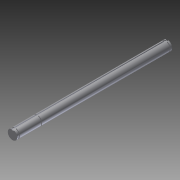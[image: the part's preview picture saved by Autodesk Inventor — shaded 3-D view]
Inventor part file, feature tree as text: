
AUTODESK INVENTOR PART (.ipt)
format: ipt  version: 2012 (Build 160160000, 160)  size: 113,152 bytes
history: native  units: in
note: dims shown in document units (in); Inventor stores cm internally (conversion verified against a paired STEP export)
features: extrude x4, sketch x4, plane x3, projected_geometry x1
ambient origin geometry x8: Origin, YZ Plane, XZ Plane, XY Plane, X Axis, Y Axis, Z Axis, Center Point
bodies: Solid1 (feature_tree)
feature tree (12):
  extrude  "Extrusion1"  Depth=6.125in TaperAngle=0.0deg
  plane  "Work Plane1"
  extrude  "Extrusion2"  Depth=0.0787in
  plane  "Work Plane2"
  extrude  "Extrusion3"  Depth=0.1481in
  plane  "Work Plane3"
  extrude  "Extrusion4"  Depth=0.03in
  sketch  "Sketch1"  dims[d0=0.375in d1=6.125in d2=0.0in]
  sketch  "Sketch2"  dims[d3=0.0787in d4=0.0787in]
  projected_geometry  "Projected Loop1"
  sketch  "Sketch3"  dims[d5=0.0394in d6=0.1481in]
  sketch  "Sketch4"  dims[d7=-0.0625in d9=0.03in d10=0.03in d11=0.0in d12=-5.145in d13=0.03in d14=0.0in d15=-0.0625in d16=0.04in d17=0.0in]
